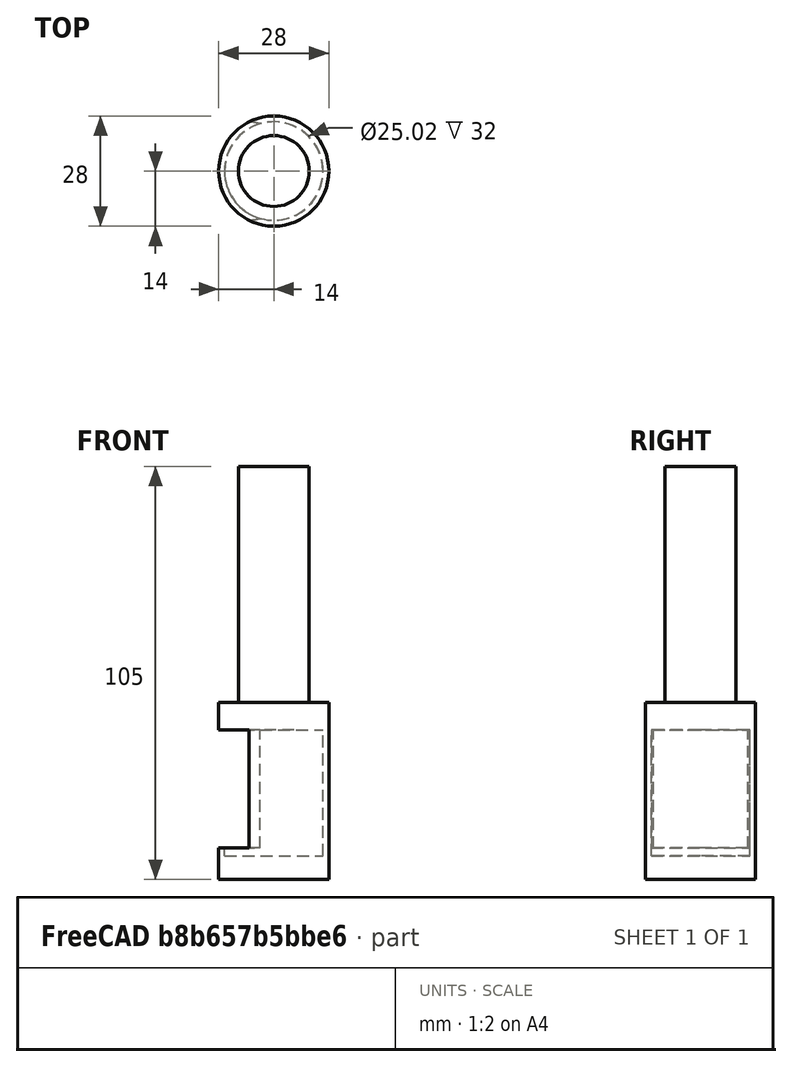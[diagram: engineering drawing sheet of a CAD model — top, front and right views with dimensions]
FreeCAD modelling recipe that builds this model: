
FCSTD DOCUMENT  (FreeCAD 0.19R24344 (Git))
Label: Holder_Magnet_Robot
License: Creative Commons Attribution-NonCommercial-ShareAlike
LicenseURL: http://creativecommons.org/licenses/by-nc-sa/4.0/
objects: Part::Cylinder×4, Part::Cut×2
note: 6 computed .brp shape members not serialized (recipe doc carries the construction recipe); baked Part::Feature solids carry a one-line shape summary decoded from their .brp

FEATURE [Part::Cylinder] Cylinder
  Angle = 360
  AttacherType = Attacher::AttachEngine3D
  Height = 60
  Radius = 9
FEATURE [Part::Cylinder] Cylinder001
  Angle = 360
  AttacherType = Attacher::AttachEngine3D
  Height = 45
  MapMode = 5
  Placement = pos=(0,0,0) rot=(1,0,0;3.14159rad)
  Radius = 14
  Support = -> [Cylinder]
FEATURE [Part::Cylinder] Cylinder002
  Angle = 360
  AttacherType = Attacher::AttachEngine3D
  AttachmentOffset = pos=(0,0,6) rot=(0,0,1;0rad)
  Height = 32
  MapMode = 5
  Placement = pos=(0,0,-39) rot=(0,0,1;3.14159rad)
  Radius = 12.51
  Support = -> [Cylinder001]
FEATURE [Part::Cut] Cut
  Base = -> Cylinder001
  Tool = -> Cylinder002
FEATURE [Part::Cylinder] Cylinder003
  Angle = 360
  AttacherType = Attacher::AttachEngine3D
  AttachmentOffset = pos=(7,0,8) rot=(0,0,1;0rad)
  Height = 30
  MapMode = 5
  Placement = pos=(-7,0,-37) rot=(0,0,1;3.14159rad)
  Radius = 12.51
  Support = -> [Cylinder001]
FEATURE [Part::Cut] Cut001
  Base = -> Cut
  Tool = -> Cylinder003
